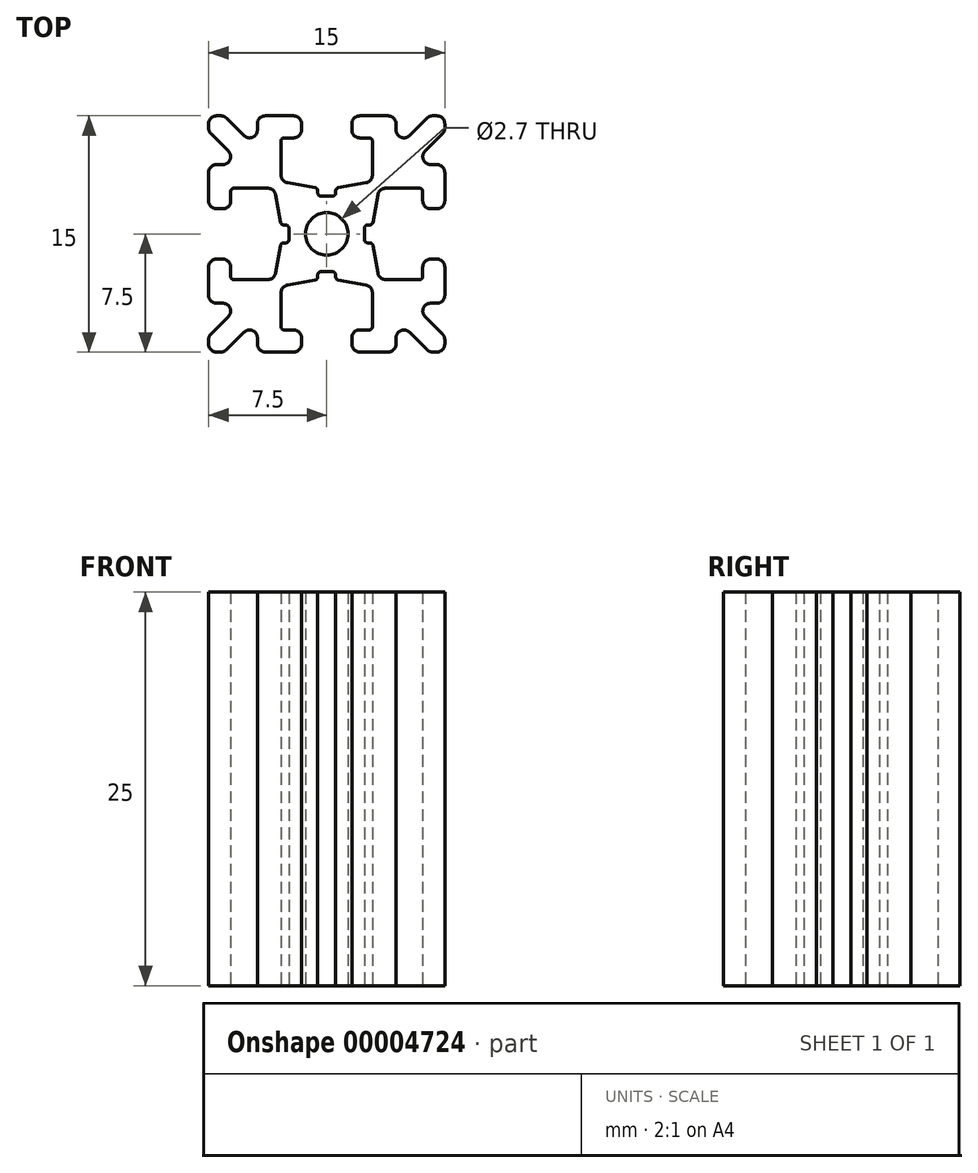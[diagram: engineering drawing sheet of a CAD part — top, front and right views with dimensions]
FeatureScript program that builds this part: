
annotation { "Feature Type Name" : "Feature", "Feature Type Description" : "" }
export const myFeature = defineFeature(function(context is Context, id is Id, definition is map)
    precondition{}
    {
        {
            var Q0;
            Q0=qCreatedBy(makeId("Top.planeOp"),FACE);
            var sketch = newSketch(context, id + "F0", { "sketchPlane" : qUnion([Q0])});
            skLineSegment(sketch, "E0", {"start": v(0, 0) * mm, "end": v(-7.5, -7.5) * mm, "construction": true});
            skArc(sketch, "E1", {"start": v(-1.35, 0) * mm, "mid": v(-1.25, -0.52) * mm, "end": v(-0.95, -0.95) * mm});
            skLineSegment(sketch, "E2", {"start": v(-7.5, -7) * mm, "end": v(-7.5, -6.72) * mm});
            skLineSegment(sketch, "E3", {"start": v(-7.35, -6.36) * mm, "end": v(-6.25, -5.26) * mm});
            skLineSegment(sketch, "E4", {"start": v(-6.6, -4.4) * mm, "end": v(-7, -4.4) * mm});
            skLineSegment(sketch, "E5", {"start": v(-7.5, -3.9) * mm, "end": v(-7.5, -2.1) * mm});
            skLineSegment(sketch, "E6", {"start": v(-7, -1.6) * mm, "end": v(-6.6, -1.6) * mm});
            skLineSegment(sketch, "E7", {"start": v(-6.1, -2.1) * mm, "end": v(-6.1, -2.7) * mm});
            skLineSegment(sketch, "E8", {"start": v(-5.9, -2.9) * mm, "end": v(-3.74, -2.9) * mm});
            skLineSegment(sketch, "E9", {"start": v(-3.25, -2.49) * mm, "end": v(-2.93, -0.73) * mm});
            skLineSegment(sketch, "E10", {"start": v(-2.73, -0.57) * mm, "end": v(-2.6, -0.57) * mm});
            skLineSegment(sketch, "E11", {"start": v(-2.4, -0.37) * mm, "end": v(-2.4, 0) * mm});
            skLineSegment(sketch, "E12", {"start": v(-2.4, 0) * mm, "end": v(-1.35, 0) * mm, "construction": true});
            skPoint(sketch, "E13.visualSharp", {"position": v(-5.4, -4.4) * mm});
            skArc(sketch, "E13.filletArc", {"start": v(-6.25, -5.26) * mm, "mid": v(-6.14, -4.71) * mm, "end": v(-6.6, -4.4) * mm});
            skPoint(sketch, "E14.visualSharp", {"position": v(-6.1, -2.9) * mm});
            skArc(sketch, "E14.filletArc", {"start": v(-6.1, -2.7) * mm, "mid": v(-6.04, -2.84) * mm, "end": v(-5.9, -2.9) * mm});
            skPoint(sketch, "E15.visualSharp", {"position": v(-6.1, -1.6) * mm});
            skArc(sketch, "E15.filletArc", {"start": v(-6.1, -2.1) * mm, "mid": v(-6.25, -1.75) * mm, "end": v(-6.6, -1.6) * mm});
            skPoint(sketch, "E16.visualSharp", {"position": v(-7.5, -1.6) * mm});
            skArc(sketch, "E16.filletArc", {"start": v(-7, -1.6) * mm, "mid": v(-7.35, -1.75) * mm, "end": v(-7.5, -2.1) * mm});
            skPoint(sketch, "E17.visualSharp", {"position": v(-7.5, -4.4) * mm});
            skArc(sketch, "E17.filletArc", {"start": v(-7.5, -3.9) * mm, "mid": v(-7.35, -4.26) * mm, "end": v(-7, -4.4) * mm});
            skPoint(sketch, "E18.visualSharp", {"position": v(-7.5, -6.51) * mm});
            skArc(sketch, "E18.filletArc", {"start": v(-7.35, -6.36) * mm, "mid": v(-7.46, -6.53) * mm, "end": v(-7.5, -6.72) * mm});
            skPoint(sketch, "E19.visualSharp", {"position": v(-3.32, -2.9) * mm});
            skArc(sketch, "E19.filletArc", {"start": v(-3.74, -2.9) * mm, "mid": v(-3.42, -2.78) * mm, "end": v(-3.25, -2.49) * mm});
            skPoint(sketch, "E20.visualSharp", {"position": v(-2.9, -0.57) * mm});
            skArc(sketch, "E20.filletArc", {"start": v(-2.73, -0.57) * mm, "mid": v(-2.86, -0.62) * mm, "end": v(-2.93, -0.73) * mm});
            skPoint(sketch, "E21.visualSharp", {"position": v(-2.4, -0.57) * mm});
            skArc(sketch, "E21.filletArc", {"start": v(-2.6, -0.57) * mm, "mid": v(-2.46, -0.51) * mm, "end": v(-2.4, -0.37) * mm});
            skLineSegment(sketch, "E22.0.MirrorCS", {"start": v(0, -2.4) * mm, "end": v(0, -1.35) * mm, "construction": true});
            skPoint(sketch, "E22.1.MirrorP", {"position": v(-4.4, -7.5) * mm});
            skArc(sketch, "E22.2.MirrorCS", {"start": v(-6.36, -7.35) * mm, "mid": v(-6.53, -7.46) * mm, "end": v(-6.72, -7.5) * mm});
            skPoint(sketch, "E22.3.MirrorP", {"position": v(-1.6, -7.5) * mm});
            skArc(sketch, "E22.4.MirrorCS", {"start": v(-1.6, -7) * mm, "mid": v(-1.75, -7.35) * mm, "end": v(-2.1, -7.5) * mm});
            skArc(sketch, "E22.5.MirrorCS", {"start": v(-0.57, -2.73) * mm, "mid": v(-0.62, -2.86) * mm, "end": v(-0.73, -2.93) * mm});
            skPoint(sketch, "E22.6.MirrorP", {"position": v(-1.6, -6.1) * mm});
            skLineSegment(sketch, "E22.7.MirrorCS", {"start": v(-3.9, -7.5) * mm, "end": v(-2.1, -7.5) * mm});
            skArc(sketch, "E22.8.MirrorCS", {"start": v(-5.26, -6.25) * mm, "mid": v(-4.71, -6.14) * mm, "end": v(-4.4, -6.6) * mm});
            skPoint(sketch, "E22.9.MirrorP", {"position": v(-0.57, -2.4) * mm});
            skPoint(sketch, "E22.10.MirrorP", {"position": v(-4.4, -5.4) * mm});
            skArc(sketch, "E22.11.MirrorCS", {"start": v(-2.7, -6.1) * mm, "mid": v(-2.84, -6.04) * mm, "end": v(-2.9, -5.9) * mm});
            skPoint(sketch, "E22.12.MirrorP", {"position": v(-0.57, -2.9) * mm});
            skLineSegment(sketch, "E22.13.MirrorCS", {"start": v(-7, -7.5) * mm, "end": v(-6.72, -7.5) * mm});
            skLineSegment(sketch, "E22.14.MirrorCS", {"start": v(-1.6, -7) * mm, "end": v(-1.6, -6.6) * mm});
            skLineSegment(sketch, "E22.15.MirrorCS", {"start": v(-6.36, -7.35) * mm, "end": v(-5.26, -6.25) * mm});
            skArc(sketch, "E22.16.MirrorCS", {"start": v(-2.1, -6.1) * mm, "mid": v(-1.75, -6.25) * mm, "end": v(-1.6, -6.6) * mm});
            skLineSegment(sketch, "E22.17.MirrorCS", {"start": v(-4.4, -6.6) * mm, "end": v(-4.4, -7) * mm});
            skArc(sketch, "E22.18.MirrorCS", {"start": v(-2.9, -3.74) * mm, "mid": v(-2.78, -3.42) * mm, "end": v(-2.49, -3.25) * mm});
            skLineSegment(sketch, "E22.19.MirrorCS", {"start": v(-2.9, -5.9) * mm, "end": v(-2.9, -3.74) * mm});
            skLineSegment(sketch, "E22.20.MirrorCS", {"start": v(-2.1, -6.1) * mm, "end": v(-2.7, -6.1) * mm});
            skArc(sketch, "E22.21.MirrorCS", {"start": v(-0.57, -2.6) * mm, "mid": v(-0.51, -2.46) * mm, "end": v(-0.37, -2.4) * mm});
            skLineSegment(sketch, "E22.22.MirrorCS", {"start": v(-0.37, -2.4) * mm, "end": v(0, -2.4) * mm});
            skPoint(sketch, "E22.23.MirrorP", {"position": v(-6.51, -7.5) * mm});
            skPoint(sketch, "E22.24.MirrorP", {"position": v(-2.9, -6.1) * mm});
            skLineSegment(sketch, "E22.25.MirrorCS", {"start": v(-2.49, -3.25) * mm, "end": v(-0.73, -2.93) * mm});
            skLineSegment(sketch, "E22.26.MirrorCS", {"start": v(-0.57, -2.73) * mm, "end": v(-0.57, -2.6) * mm});
            skArc(sketch, "E22.27.MirrorCS", {"start": v(0, -1.35) * mm, "mid": v(-0.52, -1.25) * mm, "end": v(-0.95, -0.95) * mm});
            skArc(sketch, "E22.28.MirrorCS", {"start": v(-3.9, -7.5) * mm, "mid": v(-4.26, -7.35) * mm, "end": v(-4.4, -7) * mm});
            skPoint(sketch, "E22.29.MirrorP", {"position": v(-2.9, -3.32) * mm});
            skPoint(sketch, "E23.visualSharp", {"position": v(-7.5, -7.5) * mm});
            skArc(sketch, "E23.filletArc", {"start": v(-7.5, -7) * mm, "mid": v(-7.35, -7.35) * mm, "end": v(-7, -7.5) * mm});
            skLineSegment(sketch, "E24.0.MirrorCS", {"start": v(0, 2.4) * mm, "end": v(0, 1.35) * mm, "construction": true});
            skLineSegment(sketch, "E24.1.MirrorCS", {"start": v(-2.1, 6.1) * mm, "end": v(-2.7, 6.1) * mm});
            skLineSegment(sketch, "E24.2.MirrorCS", {"start": v(-7.5, 3.9) * mm, "end": v(-7.5, 2.1) * mm});
            skLineSegment(sketch, "E24.3.MirrorCS", {"start": v(-7, 1.6) * mm, "end": v(-6.6, 1.6) * mm});
            skArc(sketch, "E24.4.MirrorCS", {"start": v(-6.1, 2.1) * mm, "mid": v(-6.25, 1.75) * mm, "end": v(-6.6, 1.6) * mm});
            skPoint(sketch, "E24.5.MirrorP", {"position": v(-3.32, 2.9) * mm});
            skPoint(sketch, "E24.6.MirrorP", {"position": v(-0.57, 2.9) * mm});
            skArc(sketch, "E24.7.MirrorCS", {"start": v(-0.57, 2.6) * mm, "mid": v(-0.51, 2.46) * mm, "end": v(-0.37, 2.4) * mm});
            skArc(sketch, "E24.8.MirrorCS", {"start": v(-2.6, 0.57) * mm, "mid": v(-2.46, 0.51) * mm, "end": v(-2.4, 0.37) * mm});
            skLineSegment(sketch, "E24.9.MirrorCS", {"start": v(-0.37, 2.4) * mm, "end": v(0, 2.4) * mm});
            skArc(sketch, "E24.10.MirrorCS", {"start": v(-6.1, 2.7) * mm, "mid": v(-6.04, 2.84) * mm, "end": v(-5.9, 2.9) * mm});
            skPoint(sketch, "E24.11.MirrorP", {"position": v(-4.4, 5.4) * mm});
            skLineSegment(sketch, "E24.12.MirrorCS", {"start": v(-2.9, 5.9) * mm, "end": v(-2.9, 3.74) * mm});
            skLineSegment(sketch, "E24.13.MirrorCS", {"start": v(-7.35, 6.36) * mm, "end": v(-6.25, 5.26) * mm});
            skPoint(sketch, "E24.14.MirrorP", {"position": v(-7.5, 6.51) * mm});
            skArc(sketch, "E24.15.MirrorCS", {"start": v(-3.74, 2.9) * mm, "mid": v(-3.42, 2.78) * mm, "end": v(-3.25, 2.49) * mm});
            skArc(sketch, "E24.16.MirrorCS", {"start": v(-2.1, 6.1) * mm, "mid": v(-1.75, 6.25) * mm, "end": v(-1.6, 6.6) * mm});
            skArc(sketch, "E24.17.MirrorCS", {"start": v(-7, 1.6) * mm, "mid": v(-7.35, 1.75) * mm, "end": v(-7.5, 2.1) * mm});
            skPoint(sketch, "E24.18.MirrorP", {"position": v(-1.6, 6.1) * mm});
            skPoint(sketch, "E24.19.MirrorP", {"position": v(-7.5, 4.4) * mm});
            skLineSegment(sketch, "E24.20.MirrorCS", {"start": v(-4.4, 6.6) * mm, "end": v(-4.4, 7) * mm});
            skArc(sketch, "E24.21.MirrorCS", {"start": v(-7.5, 3.9) * mm, "mid": v(-7.35, 4.26) * mm, "end": v(-7, 4.4) * mm});
            skPoint(sketch, "E24.22.MirrorP", {"position": v(-0.57, 2.4) * mm});
            skLineSegment(sketch, "E24.23.MirrorCS", {"start": v(-5.9, 2.9) * mm, "end": v(-3.74, 2.9) * mm});
            skArc(sketch, "E24.24.MirrorCS", {"start": v(-2.9, 3.74) * mm, "mid": v(-2.78, 3.42) * mm, "end": v(-2.49, 3.25) * mm});
            skArc(sketch, "E24.25.MirrorCS", {"start": v(-7.35, 6.36) * mm, "mid": v(-7.46, 6.53) * mm, "end": v(-7.5, 6.72) * mm});
            skPoint(sketch, "E24.26.MirrorP", {"position": v(-6.1, 2.9) * mm});
            skPoint(sketch, "E24.27.MirrorP", {"position": v(-4.4, 7.5) * mm});
            skArc(sketch, "E24.28.MirrorCS", {"start": v(-5.26, 6.25) * mm, "mid": v(-4.71, 6.14) * mm, "end": v(-4.4, 6.6) * mm});
            skArc(sketch, "E24.29.MirrorCS", {"start": v(-7.5, 7) * mm, "mid": v(-7.35, 7.35) * mm, "end": v(-7, 7.5) * mm});
            skPoint(sketch, "E24.30.MirrorP", {"position": v(-6.1, 1.6) * mm});
            skPoint(sketch, "E24.31.MirrorP", {"position": v(-2.9, 3.32) * mm});
            skPoint(sketch, "E24.32.MirrorP", {"position": v(-1.6, 7.5) * mm});
            skPoint(sketch, "E24.33.MirrorP", {"position": v(-2.9, 6.1) * mm});
            skLineSegment(sketch, "E24.34.MirrorCS", {"start": v(-3.9, 7.5) * mm, "end": v(-2.1, 7.5) * mm});
            skLineSegment(sketch, "E24.35.MirrorCS", {"start": v(-7, 7.5) * mm, "end": v(-6.72, 7.5) * mm});
            skArc(sketch, "E24.36.MirrorCS", {"start": v(-3.9, 7.5) * mm, "mid": v(-4.26, 7.35) * mm, "end": v(-4.4, 7) * mm});
            skPoint(sketch, "E24.37.MirrorP", {"position": v(-7.5, 7.5) * mm});
            skLineSegment(sketch, "E24.38.MirrorCS", {"start": v(-1.6, 7) * mm, "end": v(-1.6, 6.6) * mm});
            skLineSegment(sketch, "E24.39.MirrorCS", {"start": v(-6.36, 7.35) * mm, "end": v(-5.26, 6.25) * mm});
            skPoint(sketch, "E24.40.MirrorP", {"position": v(-7.5, 1.6) * mm});
            skArc(sketch, "E24.41.MirrorCS", {"start": v(-2.7, 6.1) * mm, "mid": v(-2.84, 6.04) * mm, "end": v(-2.9, 5.9) * mm});
            skArc(sketch, "E24.42.MirrorCS", {"start": v(-6.36, 7.35) * mm, "mid": v(-6.53, 7.46) * mm, "end": v(-6.72, 7.5) * mm});
            skLineSegment(sketch, "E24.43.MirrorCS", {"start": v(-2.49, 3.25) * mm, "end": v(-0.73, 2.93) * mm});
            skPoint(sketch, "E24.44.MirrorP", {"position": v(-2.9, 0.57) * mm});
            skLineSegment(sketch, "E24.45.MirrorCS", {"start": v(-6.6, 4.4) * mm, "end": v(-7, 4.4) * mm});
            skArc(sketch, "E24.46.MirrorCS", {"start": v(-1.6, 7) * mm, "mid": v(-1.75, 7.35) * mm, "end": v(-2.1, 7.5) * mm});
            skArc(sketch, "E24.47.MirrorCS", {"start": v(-2.73, 0.57) * mm, "mid": v(-2.86, 0.62) * mm, "end": v(-2.93, 0.73) * mm});
            skArc(sketch, "E24.48.MirrorCS", {"start": v(-6.25, 5.26) * mm, "mid": v(-6.14, 4.71) * mm, "end": v(-6.6, 4.4) * mm});
            skLineSegment(sketch, "E24.49.MirrorCS", {"start": v(-0.57, 2.73) * mm, "end": v(-0.57, 2.6) * mm});
            skLineSegment(sketch, "E24.50.MirrorCS", {"start": v(-2.73, 0.57) * mm, "end": v(-2.6, 0.57) * mm});
            skArc(sketch, "E24.51.MirrorCS", {"start": v(-1.35, 0) * mm, "mid": v(-1.25, 0.52) * mm, "end": v(-0.95, 0.95) * mm});
            skPoint(sketch, "E24.52.MirrorP", {"position": v(-2.4, 0.57) * mm});
            skPoint(sketch, "E24.53.MirrorP", {"position": v(-5.4, 4.4) * mm});
            skLineSegment(sketch, "E24.54.MirrorCS", {"start": v(-2.4, 0.37) * mm, "end": v(-2.4, 0) * mm});
            skArc(sketch, "E24.55.MirrorCS", {"start": v(0, 1.35) * mm, "mid": v(-0.52, 1.25) * mm, "end": v(-0.95, 0.95) * mm});
            skLineSegment(sketch, "E24.56.MirrorCS", {"start": v(-3.25, 2.49) * mm, "end": v(-2.93, 0.73) * mm});
            skLineSegment(sketch, "E24.57.MirrorCS", {"start": v(-6.1, 2.1) * mm, "end": v(-6.1, 2.7) * mm});
            skLineSegment(sketch, "E24.58.MirrorCS", {"start": v(-7.5, 7) * mm, "end": v(-7.5, 6.72) * mm});
            skArc(sketch, "E24.59.MirrorCS", {"start": v(-0.57, 2.73) * mm, "mid": v(-0.62, 2.86) * mm, "end": v(-0.73, 2.93) * mm});
            skPoint(sketch, "E24.60.MirrorP", {"position": v(-6.51, 7.5) * mm});
            skLineSegment(sketch, "E25.0.MirrorCS", {"start": v(7, -7.5) * mm, "end": v(6.72, -7.5) * mm});
            skLineSegment(sketch, "E25.1.MirrorCS", {"start": v(0.57, 2.73) * mm, "end": v(0.57, 2.6) * mm});
            skLineSegment(sketch, "E25.2.MirrorCS", {"start": v(0.37, 2.4) * mm, "end": v(0, 2.4) * mm});
            skLineSegment(sketch, "E25.3.MirrorCS", {"start": v(7, 7.5) * mm, "end": v(6.72, 7.5) * mm});
            skLineSegment(sketch, "E25.4.MirrorCS", {"start": v(1.6, -7) * mm, "end": v(1.6, -6.6) * mm});
            skLineSegment(sketch, "E25.5.MirrorCS", {"start": v(2.73, 0.57) * mm, "end": v(2.6, 0.57) * mm});
            skLineSegment(sketch, "E25.6.MirrorCS", {"start": v(7, 1.6) * mm, "end": v(6.6, 1.6) * mm});
            skLineSegment(sketch, "E25.7.MirrorCS", {"start": v(5.9, 2.9) * mm, "end": v(3.74, 2.9) * mm});
            skLineSegment(sketch, "E25.8.MirrorCS", {"start": v(7.35, 6.36) * mm, "end": v(6.25, 5.26) * mm});
            skArc(sketch, "E25.9.MirrorCS", {"start": v(2.7, -6.1) * mm, "mid": v(2.84, -6.04) * mm, "end": v(2.9, -5.9) * mm});
            skArc(sketch, "E25.10.MirrorCS", {"start": v(2.9, 3.74) * mm, "mid": v(2.78, 3.42) * mm, "end": v(2.49, 3.25) * mm});
            skPoint(sketch, "E25.11.MirrorP", {"position": v(1.6, -7.5) * mm});
            skPoint(sketch, "E25.12.MirrorP", {"position": v(6.1, -1.6) * mm});
            skPoint(sketch, "E25.13.MirrorP", {"position": v(2.9, 3.32) * mm});
            skPoint(sketch, "E25.14.MirrorP", {"position": v(7.5, -1.6) * mm});
            skArc(sketch, "E25.15.MirrorCS", {"start": v(1.6, 7) * mm, "mid": v(1.75, 7.35) * mm, "end": v(2.1, 7.5) * mm});
            skLineSegment(sketch, "E25.16.MirrorCS", {"start": v(6.1, -2.1) * mm, "end": v(6.1, -2.7) * mm});
            skLineSegment(sketch, "E25.17.MirrorCS", {"start": v(2.4, 0.37) * mm, "end": v(2.4, 0) * mm});
            skArc(sketch, "E25.18.MirrorCS", {"start": v(7, -1.6) * mm, "mid": v(7.35, -1.75) * mm, "end": v(7.5, -2.1) * mm});
            skArc(sketch, "E25.19.MirrorCS", {"start": v(7.5, 7) * mm, "mid": v(7.35, 7.35) * mm, "end": v(7, 7.5) * mm});
            skArc(sketch, "E25.20.MirrorCS", {"start": v(2.1, -6.1) * mm, "mid": v(1.75, -6.25) * mm, "end": v(1.6, -6.6) * mm});
            skArc(sketch, "E25.21.MirrorCS", {"start": v(6.1, 2.1) * mm, "mid": v(6.25, 1.75) * mm, "end": v(6.6, 1.6) * mm});
            skLineSegment(sketch, "E25.22.MirrorCS", {"start": v(4.4, 6.6) * mm, "end": v(4.4, 7) * mm});
            skLineSegment(sketch, "E25.23.MirrorCS", {"start": v(6.6, 4.4) * mm, "end": v(7, 4.4) * mm});
            skArc(sketch, "E25.24.MirrorCS", {"start": v(7, 1.6) * mm, "mid": v(7.35, 1.75) * mm, "end": v(7.5, 2.1) * mm});
            skArc(sketch, "E25.25.MirrorCS", {"start": v(0, -1.35) * mm, "mid": v(0.52, -1.25) * mm, "end": v(0.95, -0.95) * mm});
            skLineSegment(sketch, "E25.26.MirrorCS", {"start": v(3.9, -7.5) * mm, "end": v(2.1, -7.5) * mm});
            skLineSegment(sketch, "E25.27.MirrorCS", {"start": v(2.1, 6.1) * mm, "end": v(2.7, 6.1) * mm});
            skLineSegment(sketch, "E25.28.MirrorCS", {"start": v(2.73, -0.57) * mm, "end": v(2.6, -0.57) * mm});
            skLineSegment(sketch, "E25.29.MirrorCS", {"start": v(4.4, -6.6) * mm, "end": v(4.4, -7) * mm});
            skLineSegment(sketch, "E25.30.MirrorCS", {"start": v(3.9, 7.5) * mm, "end": v(2.1, 7.5) * mm});
            skArc(sketch, "E25.31.MirrorCS", {"start": v(0.57, -2.73) * mm, "mid": v(0.62, -2.86) * mm, "end": v(0.73, -2.93) * mm});
            skArc(sketch, "E25.32.MirrorCS", {"start": v(0.57, 2.6) * mm, "mid": v(0.51, 2.46) * mm, "end": v(0.37, 2.4) * mm});
            skPoint(sketch, "E25.33.MirrorP", {"position": v(6.51, -7.5) * mm});
            skArc(sketch, "E25.34.MirrorCS", {"start": v(3.9, -7.5) * mm, "mid": v(4.26, -7.35) * mm, "end": v(4.4, -7) * mm});
            skArc(sketch, "E25.35.MirrorCS", {"start": v(2.7, 6.1) * mm, "mid": v(2.84, 6.04) * mm, "end": v(2.9, 5.9) * mm});
            skPoint(sketch, "E25.36.MirrorP", {"position": v(0.57, -2.4) * mm});
            skPoint(sketch, "E25.37.MirrorP", {"position": v(0.57, 2.9) * mm});
            skLineSegment(sketch, "E25.38.MirrorCS", {"start": v(3.25, -2.49) * mm, "end": v(2.93, -0.73) * mm});
            skPoint(sketch, "E25.39.MirrorP", {"position": v(5.4, -4.4) * mm});
            skPoint(sketch, "E25.40.MirrorP", {"position": v(2.4, -0.57) * mm});
            skLineSegment(sketch, "E25.41.MirrorCS", {"start": v(7.5, -7) * mm, "end": v(7.5, -6.72) * mm});
            skArc(sketch, "E25.42.MirrorCS", {"start": v(7.35, 6.36) * mm, "mid": v(7.46, 6.53) * mm, "end": v(7.5, 6.72) * mm});
            skPoint(sketch, "E25.43.MirrorP", {"position": v(4.4, 7.5) * mm});
            skArc(sketch, "E25.44.MirrorCS", {"start": v(6.25, 5.26) * mm, "mid": v(6.14, 4.71) * mm, "end": v(6.6, 4.4) * mm});
            skPoint(sketch, "E25.45.MirrorP", {"position": v(6.1, -2.9) * mm});
            skPoint(sketch, "E25.46.MirrorP", {"position": v(4.4, -7.5) * mm});
            skArc(sketch, "E25.47.MirrorCS", {"start": v(6.1, 2.7) * mm, "mid": v(6.04, 2.84) * mm, "end": v(5.9, 2.9) * mm});
            skLineSegment(sketch, "E25.48.MirrorCS", {"start": v(2.1, -6.1) * mm, "end": v(2.7, -6.1) * mm});
            skArc(sketch, "E25.49.MirrorCS", {"start": v(2.73, -0.57) * mm, "mid": v(2.86, -0.62) * mm, "end": v(2.93, -0.73) * mm});
            skArc(sketch, "E25.50.MirrorCS", {"start": v(7.35, -6.36) * mm, "mid": v(7.46, -6.53) * mm, "end": v(7.5, -6.72) * mm});
            skLineSegment(sketch, "E25.51.MirrorCS", {"start": v(3.25, 2.49) * mm, "end": v(2.93, 0.73) * mm});
            skArc(sketch, "E25.52.MirrorCS", {"start": v(2.9, -3.74) * mm, "mid": v(2.78, -3.42) * mm, "end": v(2.49, -3.25) * mm});
            skArc(sketch, "E25.53.MirrorCS", {"start": v(2.6, 0.57) * mm, "mid": v(2.46, 0.51) * mm, "end": v(2.4, 0.37) * mm});
            skPoint(sketch, "E25.54.MirrorP", {"position": v(2.9, 0.57) * mm});
            skPoint(sketch, "E25.55.MirrorP", {"position": v(7.5, -6.51) * mm});
            skLineSegment(sketch, "E25.56.MirrorCS", {"start": v(2.49, 3.25) * mm, "end": v(0.73, 2.93) * mm});
            skArc(sketch, "E25.57.MirrorCS", {"start": v(1.6, -7) * mm, "mid": v(1.75, -7.35) * mm, "end": v(2.1, -7.5) * mm});
            skArc(sketch, "E25.58.MirrorCS", {"start": v(2.1, 6.1) * mm, "mid": v(1.75, 6.25) * mm, "end": v(1.6, 6.6) * mm});
            skLineSegment(sketch, "E25.59.MirrorCS", {"start": v(0.57, -2.73) * mm, "end": v(0.57, -2.6) * mm});
            skLineSegment(sketch, "E25.60.MirrorCS", {"start": v(2.4, -0.37) * mm, "end": v(2.4, 0) * mm});
            skArc(sketch, "E25.61.MirrorCS", {"start": v(7.5, -3.9) * mm, "mid": v(7.35, -4.26) * mm, "end": v(7, -4.4) * mm});
            skLineSegment(sketch, "E25.62.MirrorCS", {"start": v(5.9, -2.9) * mm, "end": v(3.74, -2.9) * mm});
            skLineSegment(sketch, "E25.63.MirrorCS", {"start": v(7.5, -3.9) * mm, "end": v(7.5, -2.1) * mm});
            skLineSegment(sketch, "E25.64.MirrorCS", {"start": v(7, -1.6) * mm, "end": v(6.6, -1.6) * mm});
            skArc(sketch, "E25.65.MirrorCS", {"start": v(1.35, 0) * mm, "mid": v(1.25, -0.52) * mm, "end": v(0.95, -0.95) * mm});
            skPoint(sketch, "E25.66.MirrorP", {"position": v(7.5, 1.6) * mm});
            skPoint(sketch, "E25.67.MirrorP", {"position": v(1.6, 6.1) * mm});
            skLineSegment(sketch, "E25.68.MirrorCS", {"start": v(6.36, -7.35) * mm, "end": v(5.26, -6.25) * mm});
            skPoint(sketch, "E25.69.MirrorP", {"position": v(2.4, 0.57) * mm});
            skPoint(sketch, "E25.70.MirrorP", {"position": v(6.1, 1.6) * mm});
            skPoint(sketch, "E25.71.MirrorP", {"position": v(3.32, -2.9) * mm});
            skPoint(sketch, "E25.72.MirrorP", {"position": v(0.57, -2.9) * mm});
            skPoint(sketch, "E25.73.MirrorP", {"position": v(7.5, 4.4) * mm});
            skArc(sketch, "E25.74.MirrorCS", {"start": v(5.26, -6.25) * mm, "mid": v(4.71, -6.14) * mm, "end": v(4.4, -6.6) * mm});
            skArc(sketch, "E25.75.MirrorCS", {"start": v(7.5, -7) * mm, "mid": v(7.35, -7.35) * mm, "end": v(7, -7.5) * mm});
            skLineSegment(sketch, "E25.76.MirrorCS", {"start": v(2.49, -3.25) * mm, "end": v(0.73, -2.93) * mm});
            skArc(sketch, "E25.77.MirrorCS", {"start": v(3.74, 2.9) * mm, "mid": v(3.42, 2.78) * mm, "end": v(3.25, 2.49) * mm});
            skArc(sketch, "E25.78.MirrorCS", {"start": v(6.36, -7.35) * mm, "mid": v(6.53, -7.46) * mm, "end": v(6.72, -7.5) * mm});
            skArc(sketch, "E25.79.MirrorCS", {"start": v(7.5, 3.9) * mm, "mid": v(7.35, 4.26) * mm, "end": v(7, 4.4) * mm});
            skArc(sketch, "E25.80.MirrorCS", {"start": v(2.73, 0.57) * mm, "mid": v(2.86, 0.62) * mm, "end": v(2.93, 0.73) * mm});
            skArc(sketch, "E25.81.MirrorCS", {"start": v(6.36, 7.35) * mm, "mid": v(6.53, 7.46) * mm, "end": v(6.72, 7.5) * mm});
            skPoint(sketch, "E25.82.MirrorP", {"position": v(4.4, -5.4) * mm});
            skPoint(sketch, "E25.83.MirrorP", {"position": v(6.51, 7.5) * mm});
            skPoint(sketch, "E25.84.MirrorP", {"position": v(2.9, -0.57) * mm});
            skLineSegment(sketch, "E25.85.MirrorCS", {"start": v(2.9, -5.9) * mm, "end": v(2.9, -3.74) * mm});
            skLineSegment(sketch, "E25.86.MirrorCS", {"start": v(6.1, 2.1) * mm, "end": v(6.1, 2.7) * mm});
            skLineSegment(sketch, "E25.87.MirrorCS", {"start": v(6.36, 7.35) * mm, "end": v(5.26, 6.25) * mm});
            skArc(sketch, "E25.88.MirrorCS", {"start": v(0.57, 2.73) * mm, "mid": v(0.62, 2.86) * mm, "end": v(0.73, 2.93) * mm});
            skArc(sketch, "E25.89.MirrorCS", {"start": v(0.57, -2.6) * mm, "mid": v(0.51, -2.46) * mm, "end": v(0.37, -2.4) * mm});
            skLineSegment(sketch, "E25.90.MirrorCS", {"start": v(2.9, 5.9) * mm, "end": v(2.9, 3.74) * mm});
            skArc(sketch, "E25.91.MirrorCS", {"start": v(0, 1.35) * mm, "mid": v(0.52, 1.25) * mm, "end": v(0.95, 0.95) * mm});
            skArc(sketch, "E25.92.MirrorCS", {"start": v(2.6, -0.57) * mm, "mid": v(2.46, -0.51) * mm, "end": v(2.4, -0.37) * mm});
            skPoint(sketch, "E25.93.MirrorP", {"position": v(4.4, 5.4) * mm});
            skPoint(sketch, "E25.94.MirrorP", {"position": v(2.9, -3.32) * mm});
            skPoint(sketch, "E25.95.MirrorP", {"position": v(2.9, 6.1) * mm});
            skPoint(sketch, "E25.96.MirrorP", {"position": v(5.4, 4.4) * mm});
            skPoint(sketch, "E25.97.MirrorP", {"position": v(3.32, 2.9) * mm});
            skArc(sketch, "E25.98.MirrorCS", {"start": v(3.74, -2.9) * mm, "mid": v(3.42, -2.78) * mm, "end": v(3.25, -2.49) * mm});
            skArc(sketch, "E25.99.MirrorCS", {"start": v(3.9, 7.5) * mm, "mid": v(4.26, 7.35) * mm, "end": v(4.4, 7) * mm});
            skPoint(sketch, "E25.100.MirrorP", {"position": v(7.5, -4.4) * mm});
            skPoint(sketch, "E25.101.MirrorP", {"position": v(6.1, 2.9) * mm});
            skArc(sketch, "E25.102.MirrorCS", {"start": v(1.35, 0) * mm, "mid": v(1.25, 0.52) * mm, "end": v(0.95, 0.95) * mm});
            skArc(sketch, "E25.103.MirrorCS", {"start": v(5.26, 6.25) * mm, "mid": v(4.71, 6.14) * mm, "end": v(4.4, 6.6) * mm});
            skPoint(sketch, "E25.104.MirrorP", {"position": v(7.5, 6.51) * mm});
            skPoint(sketch, "E25.105.MirrorP", {"position": v(2.9, -6.1) * mm});
            skArc(sketch, "E25.106.MirrorCS", {"start": v(6.25, -5.26) * mm, "mid": v(6.14, -4.71) * mm, "end": v(6.6, -4.4) * mm});
            skArc(sketch, "E25.107.MirrorCS", {"start": v(6.1, -2.1) * mm, "mid": v(6.25, -1.75) * mm, "end": v(6.6, -1.6) * mm});
            skPoint(sketch, "E25.108.MirrorP", {"position": v(1.6, 7.5) * mm});
            skPoint(sketch, "E25.109.MirrorP", {"position": v(7.5, 7.5) * mm});
            skLineSegment(sketch, "E25.110.MirrorCS", {"start": v(0.37, -2.4) * mm, "end": v(0, -2.4) * mm});
            skPoint(sketch, "E25.111.MirrorP", {"position": v(7.5, -7.5) * mm});
            skLineSegment(sketch, "E25.112.MirrorCS", {"start": v(7.5, 7) * mm, "end": v(7.5, 6.72) * mm});
            skArc(sketch, "E25.113.MirrorCS", {"start": v(6.1, -2.7) * mm, "mid": v(6.04, -2.84) * mm, "end": v(5.9, -2.9) * mm});
            skLineSegment(sketch, "E25.114.MirrorCS", {"start": v(1.6, 7) * mm, "end": v(1.6, 6.6) * mm});
            skPoint(sketch, "E25.115.MirrorP", {"position": v(1.6, -6.1) * mm});
            skLineSegment(sketch, "E25.116.MirrorCS", {"start": v(7.35, -6.36) * mm, "end": v(6.25, -5.26) * mm});
            skLineSegment(sketch, "E25.117.MirrorCS", {"start": v(7.5, 3.9) * mm, "end": v(7.5, 2.1) * mm});
            skPoint(sketch, "E25.118.MirrorP", {"position": v(0.57, 2.4) * mm});
            skLineSegment(sketch, "E25.119.MirrorCS", {"start": v(6.6, -4.4) * mm, "end": v(7, -4.4) * mm});
            skSolve(sketch);
        }
        {
            var Q0;
            Q0=makeQuery(id+"F0.imprint","IMPRINT",FACE,{"disambiguationData":[TD([[makeQuery(id+"F0.imprint","IMPRINT",EDGE,{"derivedFrom":sQuery(id+"F0.wireOp",EDGE,"E1")}),-1.0]])]});
            extrude(context, id + "F1", {"entities" : qUnion([Q0]), "depth" : 25 * mm});
        }
    });
